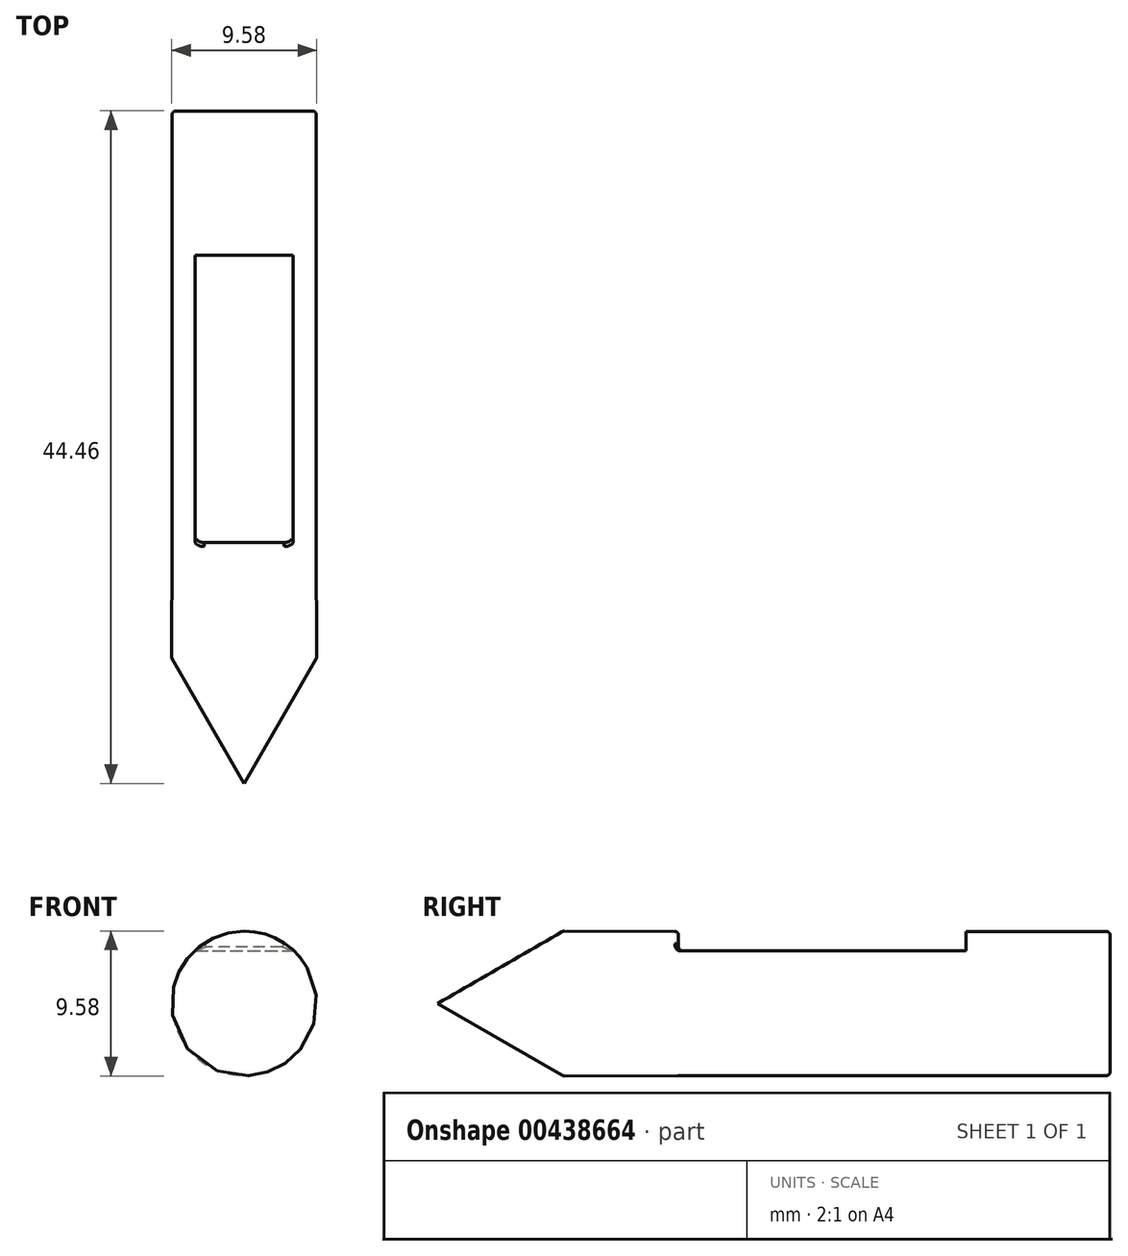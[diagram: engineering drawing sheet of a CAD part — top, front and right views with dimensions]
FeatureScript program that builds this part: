
annotation { "Feature Type Name" : "Feature", "Feature Type Description" : "" }
export const myFeature = defineFeature(function(context is Context, id is Id, definition is map)
    precondition{}
    {
        {
            var Q0;
            Q0=qCreatedBy(makeId("Front.planeOp"),FACE);
            var sketch = newSketch(context, id + "F0", { "sketchPlane" : qUnion([Q0])});
            skCircle(sketch, "E0", {"center": v(0, 0) * mm, "radius": 4.76 * mm});
            skLineSegment(sketch, "E1.0", {"start": v(-3.24, 3.5) * mm, "end": v(3.24, 3.5) * mm});
            skSolve(sketch);
        }
        {
            var Q0;
            {var subQ0=sQuery(id+"F0.wireOp",EDGE,"E1.0");Q0=makeQuery(id+"F0.imprint","IMPRINT",FACE,{"disambiguationData":[TD([[makeQuery(id+"F0.imprint","IMPRINT",EDGE,{"derivedFrom":subQ0}),-1.0]])]});}
            extrude(context, id + "F1", {"entities" : qUnion([Q0]), "depth" : 19.05 * mm});
        }
        {
            var Q0;
            Q0 = qSketchRegion(id + "F0", true);
            extrude(context, id + "F2", {"entities" : qUnion([Q0]), "operationType" : NewBodyOperationType.ADD, "oppositeDirection" : true, "depth" : 9.52 * mm});
        }
        {
            var Q0;
            Q0=qCreatedBy(makeId("Right.planeOp"),FACE);
            var sketch = newSketch(context, id + "F3", { "sketchPlane" : qUnion([Q0])});
            skLineSegment(sketch, "E2", {"start": v(-19, 0) * mm, "end": v(-34.93, 0) * mm});
            skLineSegment(sketch, "E3", {"start": v(-34.93, 0) * mm, "end": v(-26.63, 4.79) * mm});
            skLineSegment(sketch, "E4", {"start": v(-26.63, 4.79) * mm, "end": v(-19, 4.76) * mm});
            skPoint(sketch, "E5.orphan", {"position": v(-22.85, 0) * mm});
            skLineSegment(sketch, "E6", {"start": v(-19, 4.76) * mm, "end": v(-19, 0) * mm});
            skSolve(sketch);
        }
        {
            var Q0;
            Q0=makeQuery(id+"F3.imprint","IMPRINT",FACE,{"disambiguationData":[TD([[makeQuery(id+"F3.imprint","IMPRINT",EDGE,{"derivedFrom":sQuery(id+"F3.wireOp",EDGE,"E2")}),-1.0]])]});
            var Q1;
            Q1=sQuery(id+"F3.wireOp",EDGE,"E2");
            revolve(context, id + "F4", {"operationType" : NewBodyOperationType.ADD, "entities" : qUnion([Q0]), "axis" : qUnion([Q1]), "revolveType" : RevolveType.FULL});
        }
        {
            var Q0;
            Q0=makeQuery(id+"F4.opRevolve","SWEPT_EDGE",EDGE,{"disambiguationData":[OSD([sQuery(id+"F3.wireOp",EDGE,"E3"),sQuery(id+"F3.wireOp",EDGE,"E4")])]});
            var Q1;
            Q1=makeQuery(id+"F2.opExtrude","CAP_EDGE",EDGE,{"disambiguationData":[OSD([sQuery(id+"F0.wireOp",EDGE,"E0")])],"isStart":false});
            fillet(context, id + "F5", {"entities" : qUnion([Q0, Q1]), "radius" : 0.25 * mm, "tangentPropagation" : true, "allowEdgeOverflow" : false});
        }
        {
            var Q0;
            Q0=makeQuery(id+"F1.opExtrude","CAP_EDGE",EDGE,{"disambiguationData":[OSD([sQuery(id+"F0.wireOp",EDGE,"E1.0")])],"isStart":true});
            var Q1;
            Q1=makeQuery(id+"F4.boolean.opBoolean","INTERSECT",EDGE,{"derivedFrom":[makeQuery(id+"F1.opExtrude","SWEPT_FACE",FACE,{"disambiguationData":[OSD([sQuery(id+"F0.wireOp",EDGE,"E1.0")])]}),makeQuery(id+"F4.opRevolve","SWEPT_FACE",FACE,{"disambiguationData":[OSD([sQuery(id+"F3.wireOp",EDGE,"E6")])]})]});
            fillet(context, id + "F6", {"entities" : qUnion([Q0, Q1]), "radius" : 0.25 * mm, "tangentPropagation" : true, "allowEdgeOverflow" : false});
        }
        {
            var Q0;
            Q0=makeQuery(id+"F4.opRevolve","SWEPT_EDGE",EDGE,{"disambiguationData":[OSD([sQuery(id+"F3.wireOp",EDGE,"E4"),sQuery(id+"F3.wireOp",EDGE,"E6")])]});
            fillet(context, id + "F7", {"entities" : qUnion([Q0]), "radius" : 0.25 * mm, "tangentPropagation" : true, "allowEdgeOverflow" : false});
        }
    });
